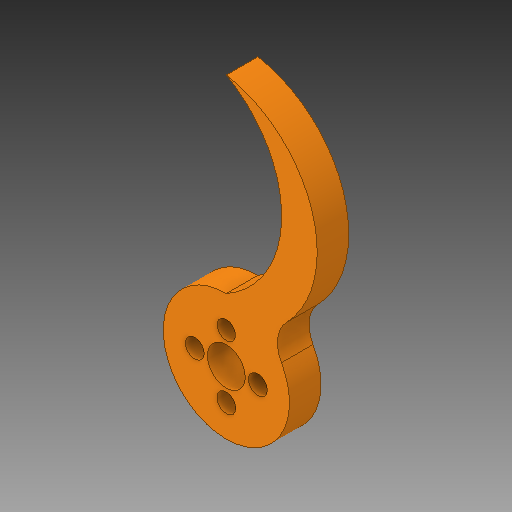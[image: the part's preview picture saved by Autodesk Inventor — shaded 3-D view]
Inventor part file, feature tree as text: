
AUTODESK INVENTOR PART (.ipt)
format: ipt  version: 2017 (Build 210142000, 142)  size: 140,800 bytes
history: native  units: in
note: dims shown in document units (in); Inventor stores cm internally (conversion verified against a paired STEP export)
features: extrude x5, sketch x5, fillet x1
ambient origin geometry x8: Origin, YZ Plane, XZ Plane, XY Plane, X Axis, Y Axis, Z Axis, Center Point
bodies: Solid1 (feature_tree)
feature tree (11):
  extrude  "Extrusion1"  Depth=0.25in TaperAngle=0.0deg
  extrude  "Extrusion2"  Depth=0.25in TaperAngle=0.0deg
  extrude  "Extrusion3"  Depth=0.25in
  extrude  "Extrusion4"  Depth=0.15in
  extrude  "Extrusion5"  Depth=0.15in
  fillet  "Fillet1"  Radius=0.25in
  sketch  "Sketch1"  dims[d0=1.0in d1=0.25in d2=0.0in]
  sketch  "Sketch2"  dims[d3=0.3in d4=0.25in d5=0.0in]
  sketch  "Sketch3"  dims[d6=0.145in d7=0.25in]
  sketch  "Sketch4"  dims[d8=0.25in d9=0.0in d10=0.15in]
  sketch  "Sketch5"  dims[d11=0.15in d12=0.15in d13=0.25in d14=0.25in d15=0.25in d16=0.25in d17=0.0in d18=1.5in d19=90.0deg d20=0.25in d21=0.0in d22=0.25in]
